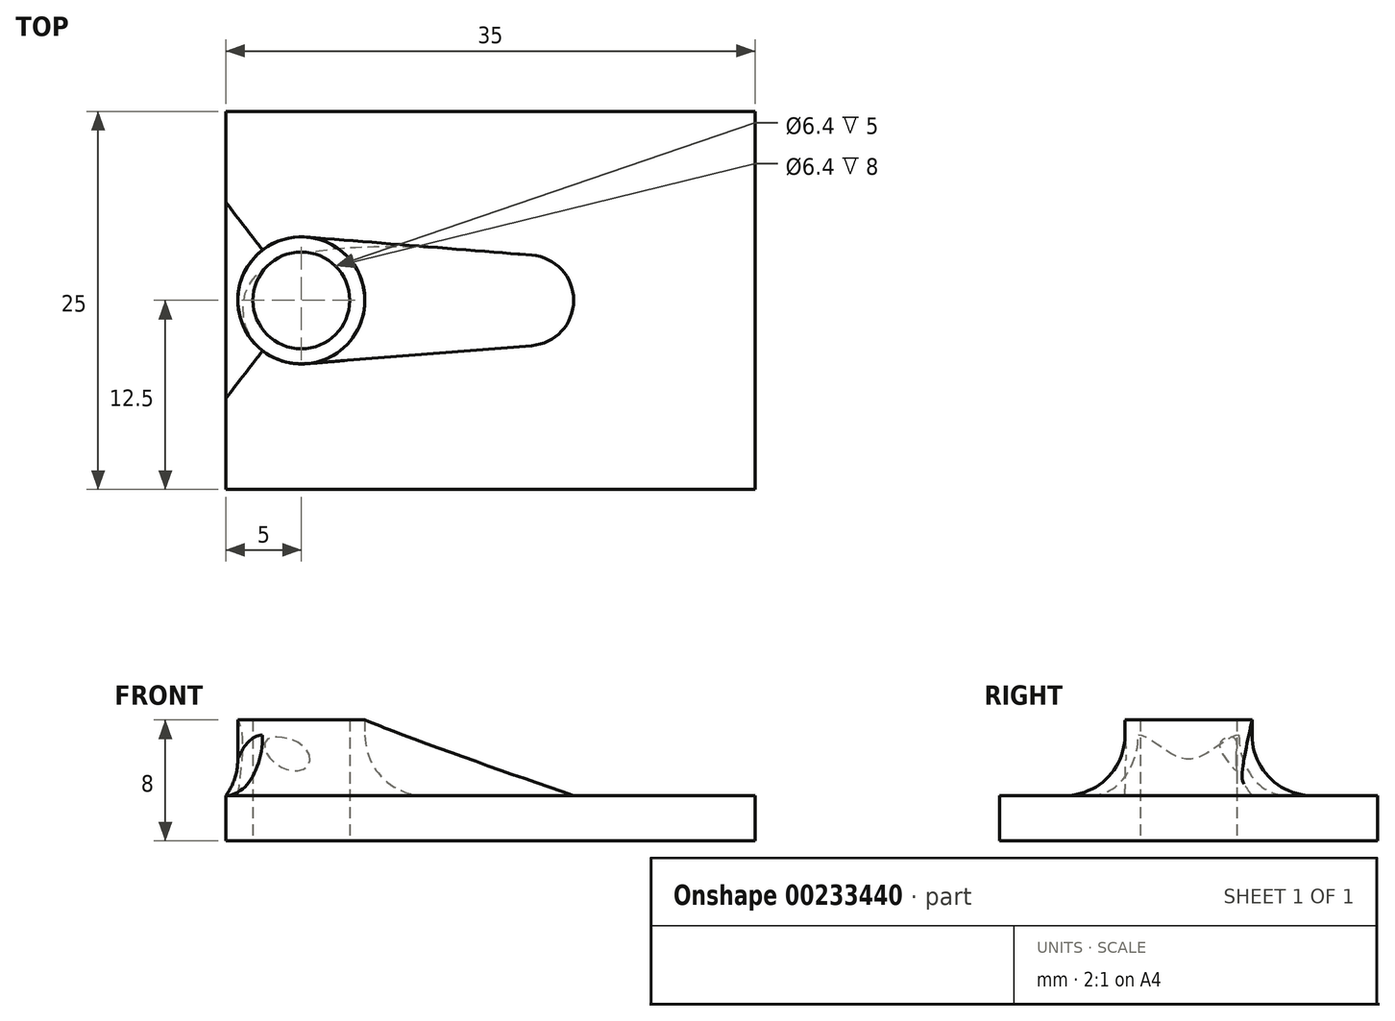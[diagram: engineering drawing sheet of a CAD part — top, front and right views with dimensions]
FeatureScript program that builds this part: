
annotation { "Feature Type Name" : "Feature", "Feature Type Description" : "" }
export const myFeature = defineFeature(function(context is Context, id is Id, definition is map)
    precondition{}
    {
        {
            var Q0;
            Q0=qCreatedBy(makeId("Top.planeOp"),FACE);
            var sketch = newSketch(context, id + "F0", { "sketchPlane" : qUnion([Q0])});
            skCircle(sketch, "E0", {"center": v(0, 0) * mm, "radius": 2 * mm});
            skCircle(sketch, "E1", {"center": v(0, 0) * mm, "radius": 3.2 * mm});
            skLineSegment(sketch, "E2.bottom", {"start": v(30, -12.5) * mm, "end": v(-5, -12.5) * mm});
            skLineSegment(sketch, "E2.top", {"start": v(30, 12.5) * mm, "end": v(-5, 12.5) * mm});
            skLineSegment(sketch, "E2.left", {"start": v(30, -12.5) * mm, "end": v(30, 12.5) * mm});
            skLineSegment(sketch, "E2.right", {"start": v(-5, -12.5) * mm, "end": v(-5, 12.5) * mm});
            skCircle(sketch, "E3.0", {"center": v(0, 0) * mm, "radius": 4.2 * mm});
            skPoint(sketch, "E4", {"position": v(-5, 0) * mm});
            skCircle(sketch, "E5", {"center": v(15, 0) * mm, "radius": 3 * mm});
            skLineSegment(sketch, "E6", {"start": v(0.34, 4.19) * mm, "end": v(15.24, 3) * mm});
            skLineSegment(sketch, "E7", {"start": v(0.34, -4.19) * mm, "end": v(15.24, -3) * mm});
            skSolve(sketch);
        }
        {
            var Q0;
            Q0=makeQuery(id+"F0.imprint","IMPRINT",FACE,{"disambiguationData":[TD([[makeQuery(id+"F0.imprint","IMPRINT",EDGE,{"derivedFrom":sQuery(id+"F0.wireOp",EDGE,"E2.bottom")}),-1.0]])]});
            var Q1;
            {var subQ0=sQuery(id+"F0.wireOp",EDGE,"E5");var subQ1=makeQuery(id+"F0.imprint","INTERSECT",VERTEX,{"derivedFrom":[subQ0,sQuery(id+"F0.wireOp",EDGE,"E6")]});Q1=makeQuery(id+"F0.imprint","IMPRINT",FACE,{"disambiguationData":[TD([[makeQuery(id+"F0.imprint","IMPRINT",EDGE,{"disambiguationData":[TD([[subQ1,-1.0]])],"derivedFrom":subQ0}),1.0]])]});}
            var Q2;
            {var subQ0=sQuery(id+"F0.wireOp",EDGE,"E6");Q2=makeQuery(id+"F0.imprint","IMPRINT",FACE,{"disambiguationData":[TD([[makeQuery(id+"F0.imprint","IMPRINT",EDGE,{"derivedFrom":subQ0}),-1.0]])]});}
            var Q3;
            Q3=makeQuery(id+"F0.imprint","IMPRINT",FACE,{"disambiguationData":[TD([[makeQuery(id+"F0.imprint","IMPRINT",EDGE,{"derivedFrom":sQuery(id+"F0.wireOp",EDGE,"E1")}),-1.0]])]});
            var Q4;
            Q4=makeQuery(id+"F0.imprint","IMPRINT",FACE,{"disambiguationData":[TD([[makeQuery(id+"F0.imprint","IMPRINT",EDGE,{"derivedFrom":sQuery(id+"F0.wireOp",EDGE,"E0")}),-1.0]])]});
            extrude(context, id + "F6", {"entities" : qUnion([Q0, Q1, Q2, Q3, Q4]), "depth" : 3 * mm});
        }
        {
            var Q0;
            Q0=makeQuery(id+"F0.imprint","IMPRINT",FACE,{"disambiguationData":[TD([[makeQuery(id+"F0.imprint","IMPRINT",EDGE,{"derivedFrom":sQuery(id+"F0.wireOp",EDGE,"E1")}),-1.0]])]});
            extrude(context, id + "F1", {"entities" : qUnion([Q0]), "operationType" : NewBodyOperationType.ADD, "depth" : 8 * mm});
        }
        {
            var Q0;
            {var subQ0=sQuery(id+"F0.wireOp",EDGE,"E2.right");var subQ1=sQuery(id+"F0.wireOp",EDGE,"E2.left");var subQ2=sQuery(id+"F0.wireOp",EDGE,"E2.top");var subQ3=sQuery(id+"F0.wireOp",EDGE,"E2.bottom");Q0=makeQuery(id+"F1.boolean.opBoolean","SPLIT",FACE,{"disambiguationData":[TD([makeQuery(id+"F6.opExtrude","SWEPT_FACE",FACE,{"disambiguationData":[OSD([subQ3])]})])],"derivedFrom":makeQuery(id+"F6.opExtrude","CAP_FACE",FACE,{"disambiguationData":[OSD([sQuery(id+"F0.wireOp",EDGE,"E0"),subQ3,subQ2,subQ1,subQ0])],"isStart":false})});}
            cPlane(context, id + "F2", {"entities" : qUnion([Q0]), "cplaneType" : CPlaneType.OFFSET, "offset" : 0 * mm, "width" : 150 * mm, "height" : 150 * mm});
        }
        {
            var Q0;
            Q0=qCreatedBy(id+"F2.planeOp",FACE);
            var sketch = newSketch(context, id + "F7", { "sketchPlane" : qUnion([Q0])});
            skArc(sketch, "E8.0", {"start": v(15.24, -3) * mm, "mid": v(18, 0) * mm, "end": v(15.24, 3) * mm});
            skLineSegment(sketch, "E9.0", {"start": v(0.34, -4.19) * mm, "end": v(15.24, -3) * mm});
            skLineSegment(sketch, "E10.0", {"start": v(0.34, 4.19) * mm, "end": v(15.24, 3) * mm});
            skArc(sketch, "E11.0", {"start": v(0.34, 4.19) * mm, "mid": v(-4.2, 0) * mm, "end": v(0.34, -4.19) * mm});
            skSolve(sketch);
        }
        {
            var Q0;
            Q0=makeQuery(id+"F1.opExtrude","CAP_FACE",FACE,{"disambiguationData":[OSD([sQuery(id+"F0.wireOp",EDGE,"E1"),sQuery(id+"F0.wireOp",EDGE,"E3.0")])],"isStart":false});
            cPlane(context, id + "F3", {"entities" : qUnion([Q0]), "cplaneType" : CPlaneType.OFFSET, "offset" : 0 * mm, "width" : 150 * mm, "height" : 150 * mm});
        }
        {
            var Q0;
            Q0=qCreatedBy(id+"F3.planeOp",FACE);
            var sketch = newSketch(context, id + "F4", { "sketchPlane" : qUnion([Q0])});
            skCircle(sketch, "E12.0", {"center": v(0, 0) * mm, "radius": 4.2 * mm});
            skSolve(sketch);
        }
        {
            var Q0;
            Q0=makeQuery(id+"F7.imprint","IMPRINT",FACE,{"disambiguationData":[TD([[makeQuery(id+"F7.imprint","IMPRINT",EDGE,{"derivedFrom":sQuery(id+"F7.wireOp",EDGE,"E8.0")}),1.0]])]});
            var Q1;
            Q1=makeQuery(id+"F4.imprint","IMPRINT",FACE,{"disambiguationData":[TD([[makeQuery(id+"F4.imprint","IMPRINT",EDGE,{"derivedFrom":sQuery(id+"F4.wireOp",EDGE,"E12.0")}),1.0]])]});
            var Q2;
            Q2 = qBodyType(qCreatedBy(id + "F7" ,EDGE), BodyType.WIRE);
            var Q3;
            Q3 = qBodyType(qCreatedBy(id + "FIAlYlMUEZcUdSAsv_2" ,EDGE), BodyType.WIRE);
            loft(context, id + "F8", {"sheetProfilesArray" : [{ "sheetProfileEntities" : qUnion([Q0]) }, { "sheetProfileEntities" : qUnion([Q1]) }], "wireProfilesArray" : [{ "wireProfileEntities" : qUnion([Q2]) }, { "wireProfileEntities" : qUnion([Q3]) }]});
        }
        {
            var Q0;
            Q0=makeQuery(id+"F0.imprint","IMPRINT",FACE,{"disambiguationData":[TD([[makeQuery(id+"F0.imprint","IMPRINT",EDGE,{"derivedFrom":sQuery(id+"F0.wireOp",EDGE,"E0")}),-1.0]])]});
            var Q1;
            Q1=makeQuery(id+"F0.imprint","IMPRINT",FACE,{"disambiguationData":[TD([[makeQuery(id+"F0.imprint","IMPRINT",EDGE,{"derivedFrom":sQuery(id+"F0.wireOp",EDGE,"E0")}),1.0]])]});
            extrude(context, id + "F9", {"entities" : qUnion([Q0, Q1]), "operationType" : NewBodyOperationType.REMOVE, "depth" : 25 * mm});
        }
        {
            var Q0;
            Q0=makeQuery(id+"F8.opLoft","MID_CAP_EDGE",EDGE,{"disambiguationData":[OSD([sQuery(id+"F7.wireOp",EDGE,"E8.0"),sQuery(id+"F7.wireOp",EDGE,"E9.0"),sQuery(id+"F7.wireOp",EDGE,"E11.0")])],"capPos":0.0});
            var Q1;
            Q1=makeQuery(id+"F1.boolean.opBoolean","INTERSECT",EDGE,{"derivedFrom":[makeQuery(id+"F6.opExtrude","CAP_FACE",FACE,{"disambiguationData":[OSD([sQuery(id+"F0.wireOp",EDGE,"E0"),sQuery(id+"F0.wireOp",EDGE,"E2.bottom"),sQuery(id+"F0.wireOp",EDGE,"E2.top"),sQuery(id+"F0.wireOp",EDGE,"E2.left"),sQuery(id+"F0.wireOp",EDGE,"E2.right")])],"isStart":false}),makeQuery(id+"F1.opExtrude","SWEPT_FACE",FACE,{"disambiguationData":[OSD([sQuery(id+"F0.wireOp",EDGE,"E3.0")])]})]});
            var Q2;
            Q2=makeQuery(id+"F8.opLoft","MID_CAP_EDGE",EDGE,{"disambiguationData":[OSD([sQuery(id+"F7.wireOp",EDGE,"E8.0"),sQuery(id+"F7.wireOp",EDGE,"E10.0"),sQuery(id+"F7.wireOp",EDGE,"E11.0")])],"capPos":0.0});
            var Q3;
            Q3=makeQuery(id+"F8.opLoft","MID_CAP_EDGE",EDGE,{"disambiguationData":[OSD([sQuery(id+"F7.wireOp",EDGE,"E8.0"),sQuery(id+"F7.wireOp",EDGE,"E9.0"),sQuery(id+"F7.wireOp",EDGE,"E10.0")])],"capPos":0.0});
            fillet(context, id + "F5", {"entities" : qUnion([Q0, Q1, Q2, Q3]), "radius" : 4 * mm, "tangentPropagation" : true, "allowEdgeOverflow" : false});
        }
    });
